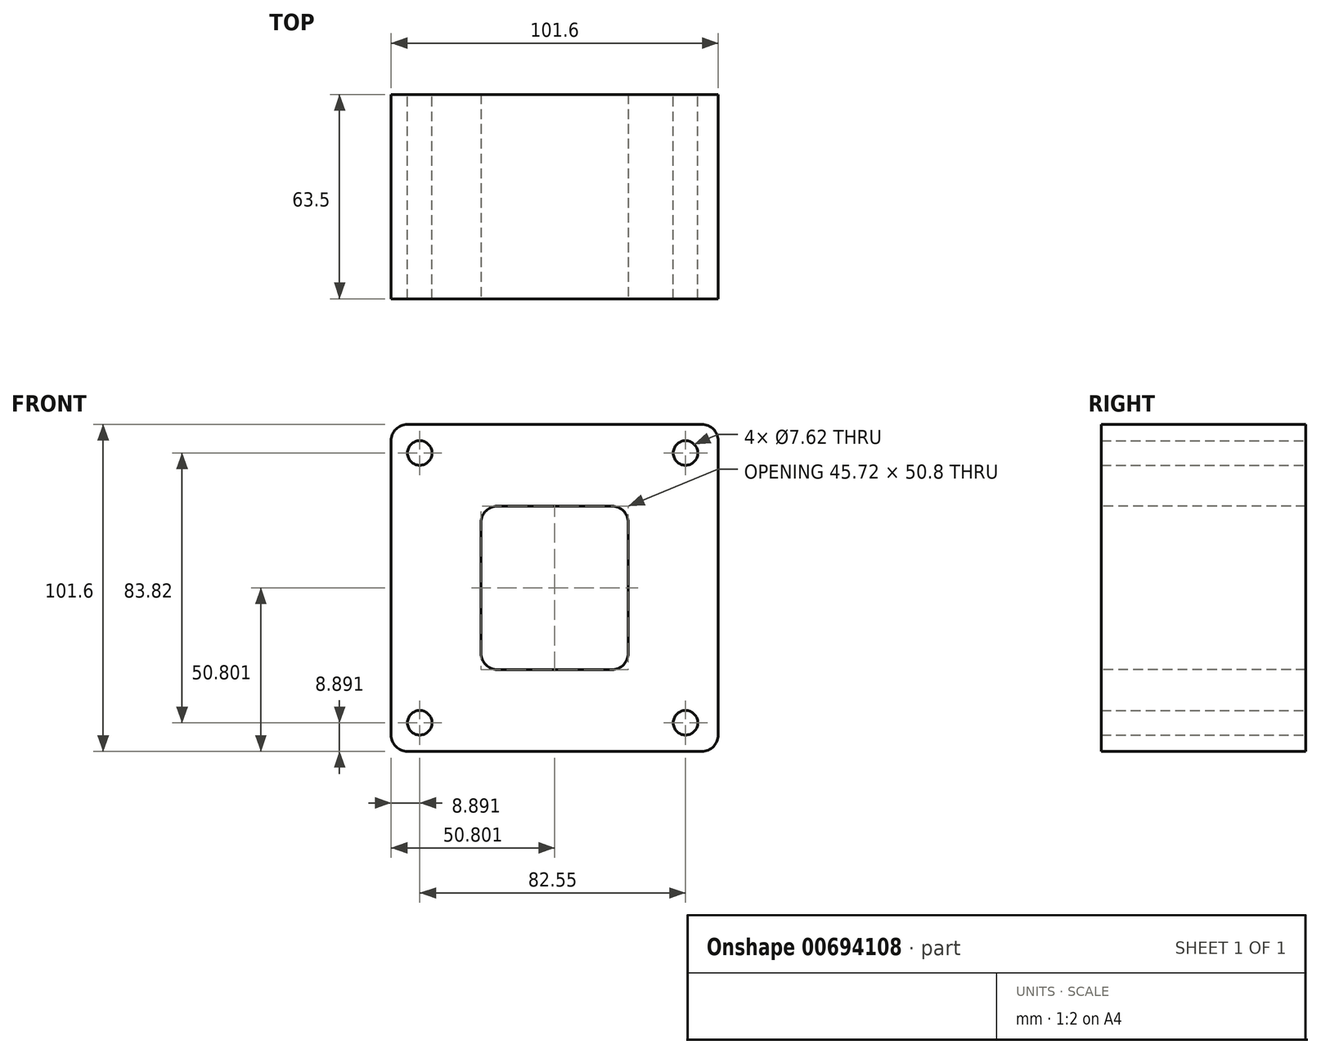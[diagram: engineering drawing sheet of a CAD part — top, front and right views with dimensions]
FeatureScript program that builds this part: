
annotation { "Feature Type Name" : "Feature", "Feature Type Description" : "" }
export const myFeature = defineFeature(function(context is Context, id is Id, definition is map)
    precondition{}
    {
        {
            var Q0;
            Q0=qCreatedBy(makeId("Front.planeOp"),FACE);
            var sketch = newSketch(context, id + "F0", { "sketchPlane" : qUnion([Q0])});
            skLineSegment(sketch, "E0.bottom", {"start": v(-58.2, 68.8) * mm, "end": v(43.4, 68.8) * mm});
            skLineSegment(sketch, "E0.top", {"start": v(-58.2, -32.8) * mm, "end": v(43.4, -32.8) * mm});
            skLineSegment(sketch, "E0.left", {"start": v(-58.2, 68.8) * mm, "end": v(-58.2, -32.8) * mm});
            skLineSegment(sketch, "E0.right", {"start": v(43.4, 68.8) * mm, "end": v(43.4, -32.8) * mm});
            skCircle(sketch, "E1", {"center": v(-49.32, 59.91) * mm, "radius": 3.81 * mm});
            skCircle(sketch, "E2.1.0.0", {"center": v(33.23, 59.91) * mm, "radius": 3.81 * mm});
            skLineSegment(sketch, "E2.direction1", {"start": v(-49.32, 59.91) * mm, "end": v(33.23, 59.91) * mm, "construction": true});
            skCircle(sketch, "E3", {"center": v(-49.32, -23.9) * mm, "radius": 3.81 * mm});
            skCircle(sketch, "E4.1.0.0", {"center": v(33.23, -23.9) * mm, "radius": 3.81 * mm});
            skLineSegment(sketch, "E4.direction1", {"start": v(-49.32, -23.9) * mm, "end": v(33.23, -23.9) * mm, "construction": true});
            skSolve(sketch);
        }
        {
            var Q0;
            Q0=makeQuery(id+"F0.imprint","IMPRINT",FACE,{"disambiguationData":[TD([[makeQuery(id+"F0.imprint","IMPRINT",EDGE,{"derivedFrom":sQuery(id+"F0.wireOp",EDGE,"E0.bottom")}),-1.0]])]});
            extrude(context, id + "F1", {"entities" : qUnion([Q0]), "depth" : 63.5 * mm, "offsetDistance" : 25.4 * mm});
        }
        {
            var Q0;
            Q0=makeQuery(id+"F1.opExtrude","CAP_FACE",FACE,{"disambiguationData":[OSD([sQuery(id+"F0.wireOp",EDGE,"E0.bottom"),sQuery(id+"F0.wireOp",EDGE,"E0.top"),sQuery(id+"F0.wireOp",EDGE,"E0.left"),sQuery(id+"F0.wireOp",EDGE,"E0.right")])],"isStart":false});
            var sketch = newSketch(context, id + "F2", { "sketchPlane" : qUnion([Q0])});
            skLineSegment(sketch, "E5.bottom", {"start": v(-30.27, 43.4) * mm, "end": v(15.45, 43.4) * mm});
            skLineSegment(sketch, "E5.top", {"start": v(-30.27, -7.4) * mm, "end": v(15.45, -7.4) * mm});
            skLineSegment(sketch, "E5.left", {"start": v(-30.27, 43.4) * mm, "end": v(-30.27, -7.4) * mm});
            skLineSegment(sketch, "E5.right", {"start": v(15.45, 43.4) * mm, "end": v(15.45, -7.4) * mm});
            skSolve(sketch);
        }
        {
            var Q0;
            Q0=makeQuery(id+"F2.imprint","IMPRINT",FACE,{"disambiguationData":[TD([[makeQuery(id+"F2.imprint","IMPRINT",EDGE,{"derivedFrom":sQuery(id+"F2.wireOp",EDGE,"E5.bottom")}),-1.0]])]});
            extrude(context, id + "F3", {"entities" : qUnion([Q0]), "operationType" : NewBodyOperationType.REMOVE, "oppositeDirection" : true, "depth" : 63.5 * mm, "offsetDistance" : 25.4 * mm});
        }
        {
            var Q0;
            Q0=makeQuery(id+"F1.opExtrude","SWEPT_EDGE",EDGE,{"disambiguationData":[OSD([sQuery(id+"F0.wireOp",EDGE,"E0.bottom"),sQuery(id+"F0.wireOp",EDGE,"E0.left")])]});
            var Q1;
            Q1=makeQuery(id+"F1.opExtrude","SWEPT_EDGE",EDGE,{"disambiguationData":[OSD([sQuery(id+"F0.wireOp",EDGE,"E0.top"),sQuery(id+"F0.wireOp",EDGE,"E0.left")])]});
            var Q2;
            Q2=makeQuery(id+"F1.opExtrude","SWEPT_EDGE",EDGE,{"disambiguationData":[OSD([sQuery(id+"F0.wireOp",EDGE,"E0.top"),sQuery(id+"F0.wireOp",EDGE,"E0.right")])]});
            var Q3;
            Q3=makeQuery(id+"F1.opExtrude","SWEPT_EDGE",EDGE,{"disambiguationData":[OSD([sQuery(id+"F0.wireOp",EDGE,"E0.bottom"),sQuery(id+"F0.wireOp",EDGE,"E0.right")])]});
            fillet(context, id + "F4", {"entities" : qUnion([Q0, Q1, Q2, Q3]), "radius" : 5.08 * mm, "tangentPropagation" : true, "allowEdgeOverflow" : false});
        }
        {
            var Q0;
            Q0=makeQuery(id+"F3.boolean.opBoolean","COPY",EDGE,{"derivedFrom":makeQuery(id+"F3.opExtrude","SWEPT_EDGE",EDGE,{"disambiguationData":[OSD([sQuery(id+"F2.wireOp",EDGE,"E5.bottom"),sQuery(id+"F2.wireOp",EDGE,"E5.left")])]})});
            fillet(context, id + "F5", {"entities" : qUnion([Q0]), "radius" : 5.08 * mm, "tangentPropagation" : true, "allowEdgeOverflow" : false});
        }
        {
            var Q0;
            Q0=makeQuery(id+"F3.boolean.opBoolean","COPY",EDGE,{"derivedFrom":makeQuery(id+"F3.opExtrude","SWEPT_EDGE",EDGE,{"disambiguationData":[OSD([sQuery(id+"F2.wireOp",EDGE,"E5.top"),sQuery(id+"F2.wireOp",EDGE,"E5.left")])]})});
            var Q1;
            Q1=makeQuery(id+"F3.boolean.opBoolean","COPY",EDGE,{"derivedFrom":makeQuery(id+"F3.opExtrude","SWEPT_EDGE",EDGE,{"disambiguationData":[OSD([sQuery(id+"F2.wireOp",EDGE,"E5.bottom"),sQuery(id+"F2.wireOp",EDGE,"E5.right")])]})});
            var Q2;
            Q2=makeQuery(id+"F3.boolean.opBoolean","COPY",EDGE,{"derivedFrom":makeQuery(id+"F3.opExtrude","SWEPT_EDGE",EDGE,{"disambiguationData":[OSD([sQuery(id+"F2.wireOp",EDGE,"E5.top"),sQuery(id+"F2.wireOp",EDGE,"E5.right")])]})});
            fillet(context, id + "F6", {"entities" : qUnion([Q0, Q1, Q2]), "radius" : 5.08 * mm, "tangentPropagation" : true, "allowEdgeOverflow" : false});
        }
    });
